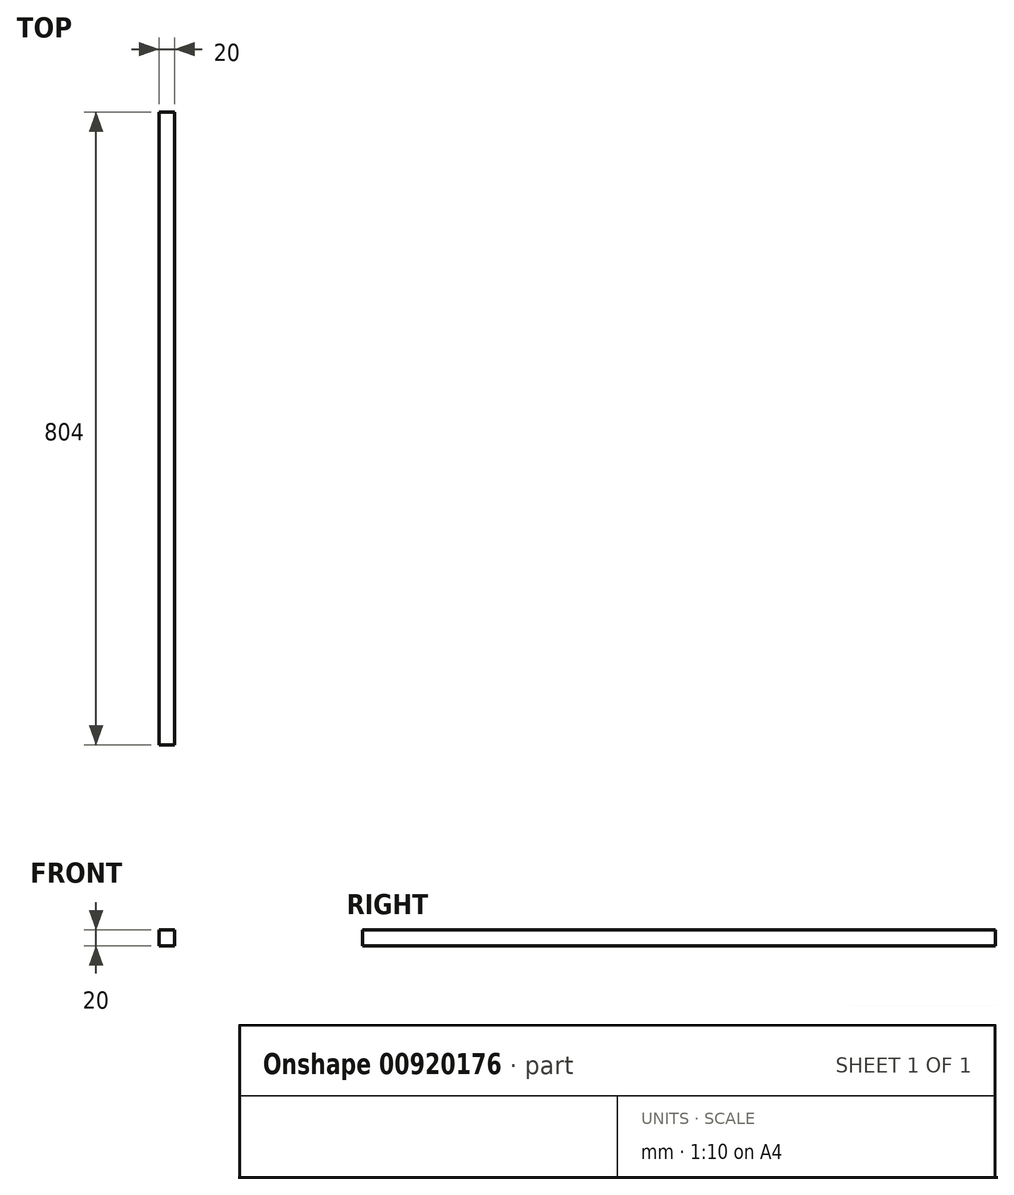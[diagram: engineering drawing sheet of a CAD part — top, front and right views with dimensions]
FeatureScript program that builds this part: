
annotation { "Feature Type Name" : "Feature", "Feature Type Description" : "" }
export const myFeature = defineFeature(function(context is Context, id is Id, definition is map)
    precondition{}
    {
        {
            var Q0;
            Q0=qCreatedBy(makeId("Front.planeOp"),FACE);
            var sketch = newSketch(context, id + "F0", { "sketchPlane" : qUnion([Q0])});
            skLineSegment(sketch, "E0.bottom", {"start": v(-1.9, 12.82) * mm, "end": v(18.1, 12.82) * mm});
            skLineSegment(sketch, "E0.top", {"start": v(-1.9, -7.18) * mm, "end": v(18.1, -7.18) * mm});
            skLineSegment(sketch, "E0.left", {"start": v(-1.9, 12.82) * mm, "end": v(-1.9, -7.18) * mm});
            skLineSegment(sketch, "E0.right", {"start": v(18.1, 12.82) * mm, "end": v(18.1, -7.18) * mm});
            skSolve(sketch);
        }
        {
            var Q0;
            Q0=qSketchRegion(id+"F0",true);
            extrude(context, id + "F1", {"entities" : qUnion([Q0]), "depth" : 804 * mm, "offsetDistance" : 25 * mm});
        }
    });
